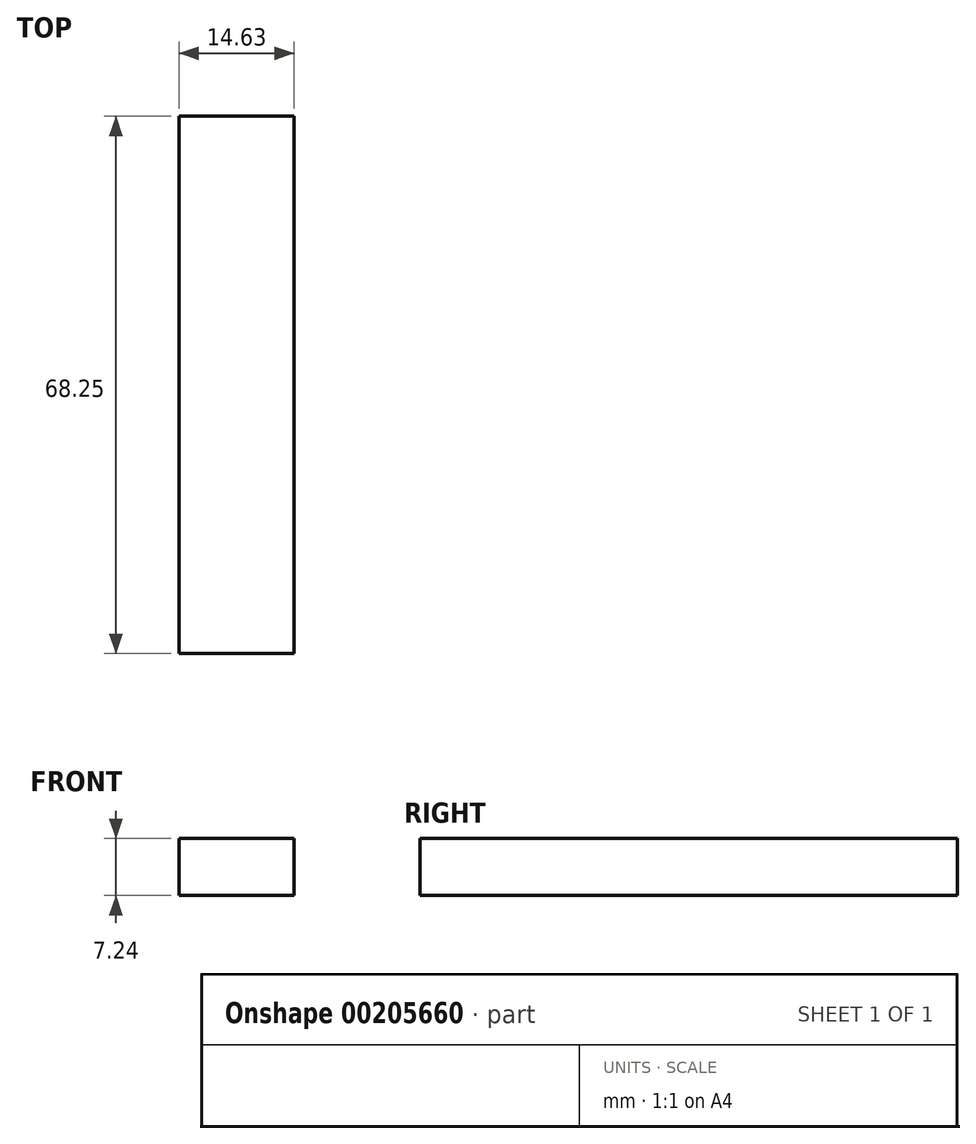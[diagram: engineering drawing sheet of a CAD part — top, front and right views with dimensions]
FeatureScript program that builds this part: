
annotation { "Feature Type Name" : "Feature", "Feature Type Description" : "" }
export const myFeature = defineFeature(function(context is Context, id is Id, definition is map)
    precondition{}
    {
        {
            var Q0;
            Q0=qCreatedBy(makeId("Right.planeOp"),FACE);
            var sketch = newSketch(context, id + "F0", { "sketchPlane" : qUnion([Q0])});
            skLineSegment(sketch, "E0.bottom", {"start": v(15.86, 3.62) * mm, "end": v(-52.4, 3.63) * mm});
            skLineSegment(sketch, "E0.top", {"start": v(15.86, -3.63) * mm, "end": v(-52.4, -3.62) * mm});
            skLineSegment(sketch, "E0.left", {"start": v(15.86, 3.63) * mm, "end": v(15.86, -3.63) * mm});
            skLineSegment(sketch, "E0.right", {"start": v(-52.4, 3.63) * mm, "end": v(-52.4, -3.63) * mm});
            skLineSegment(sketch, "E1", {"start": v(0, 3.63) * mm, "end": v(0, -3.63) * mm, "construction": true});
            skSolve(sketch);
        }
        {
            var Q0;
            Q0=makeQuery(id+"F0.imprint","IMPRINT",FACE,{"disambiguationData":[TD([[makeQuery(id+"F0.imprint","IMPRINT",EDGE,{"derivedFrom":sQuery(id+"F0.wireOp",EDGE,"E0.bottom")}),1.0]])]});
            extrude(context, id + "F1", {"entities" : qUnion([Q0]), "oppositeDirection" : true, "depth" : (9.18 + (10.9 / 2)) * mm});
        }
    });
